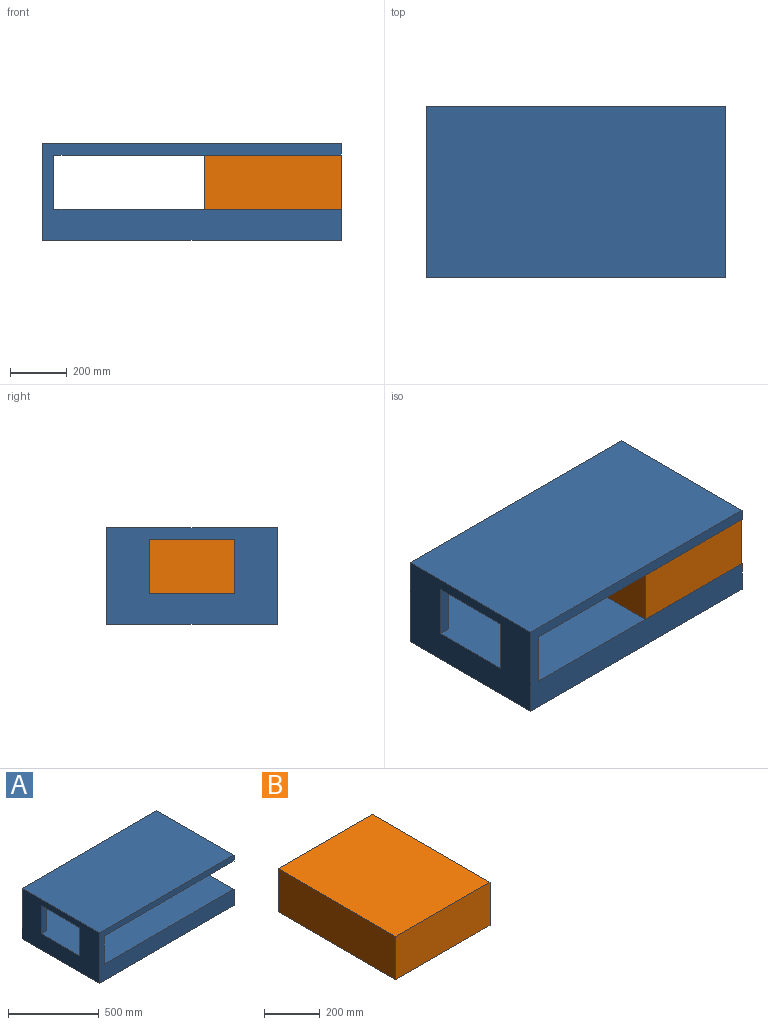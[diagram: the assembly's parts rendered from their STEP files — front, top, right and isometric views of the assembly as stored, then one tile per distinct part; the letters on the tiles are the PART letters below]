
ASSEMBLY  parts=2 mates=1
PART A: 13 faces, bbox 1050x600x340 mm
  f0: plane 190x150mm, normal (1,0,0), area 28500mm2, adj f2,f4,f10,f11
  f1: plane 600x110mm, normal (1,0,0), area 66000mm2, adj f2,f8,f9,f10
  f2: plane 1050x600mm, normal (0,0,1), area 618000mm2, adj f0,f1,f3,f7,f9,f10,f11,f12
  f3: plane 190x150mm, normal (1,0,0), area 28500mm2, adj f2,f4,f9,f12
  f4: plane 1050x600mm, normal (0,0,-1), area 618000mm2, adj f0,f3,f5,f7,f9,f10,f11,f12
  f5: plane 600x40mm, normal (1,0,0), area 24000mm2, adj f4,f6,f9,f10
  f6: plane 1050x600mm, normal (0,0,1), area 630000mm2, adj f5,f7,f9,f10
  f7: plane 600x340mm, normal (-1,0,0), area 147000mm2, adj f2,f4,f6,f8,f9,f10,f11,f12
  f8: plane 1050x600mm, normal (0,0,-1), area 630000mm2, adj f1,f7,f9,f10
  f9: plane 1050x340mm, normal (0,-1,0), area 165100mm2, adj f1,f2,f3,f4,f5,f6,f7,f8
  f10: plane 1050x340mm, normal (0,1,0), area 165100mm2, adj f0,f1,f2,f4,f5,f6,f7,f8
  f11: plane 190x40mm, normal (0,-1,0), area 7600mm2, adj f0,f2,f4,f7
  f12: plane 190x40mm, normal (0,1,0), area 7600mm2, adj f2,f3,f4,f7
PART B: 6 faces, bbox 480x600x190 mm
  f0: plane 480x190mm, normal (0,-1,0), area 91200mm2, adj f1,f3,f4,f5
  f1: plane 600x190mm, normal (-1,0,0), area 114000mm2, adj f0,f2,f3,f4
  f2: plane 480x190mm, normal (0,1,0), area 91200mm2, adj f1,f3,f4,f5
  f3: plane 600x480mm, normal (0,0,-1), area 288000mm2, adj f0,f1,f2,f5
  f4: plane 600x480mm, normal (0,0,1), area 288000mm2, adj f0,f1,f2,f5
  f5: plane 600x190mm, normal (1,0,0), area 114000mm2, adj f0,f2,f3,f4
PLACE A at identity
PLACE B at identity
MATE revolute B.f4 <-> A.f4  axis (0,0,1) through (975,-525,300)mm
